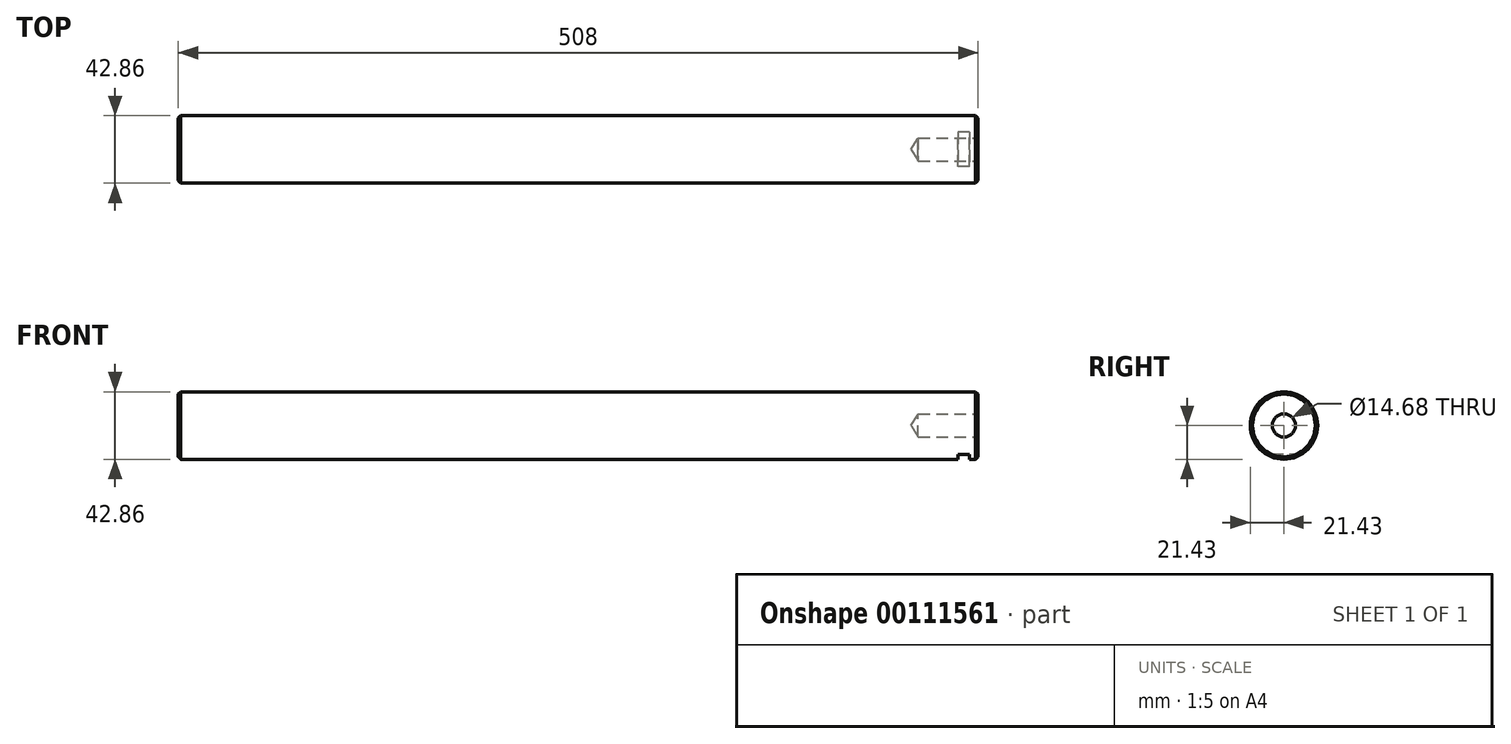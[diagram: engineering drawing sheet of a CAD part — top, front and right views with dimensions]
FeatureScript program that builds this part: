
annotation { "Feature Type Name" : "Feature", "Feature Type Description" : "" }
export const myFeature = defineFeature(function(context is Context, id is Id, definition is map)
    precondition{}
    {
        {
            var Q0;
            Q0=qCreatedBy(makeId("Right.planeOp"),FACE);
            var sketch = newSketch(context, id + "F0", { "sketchPlane" : qUnion([Q0])});
            skCircle(sketch, "E0", {"center": v(0, 0) * mm, "radius": 21.43 * mm});
            skSolve(sketch);
        }
        {
            var Q0;
            Q0 = qSketchRegion(id + "F0", true);
            extrude(context, id + "F1", {"entities" : qUnion([Q0]), "endBound" : BoundingType.SYMMETRIC, "depth" : 508 * mm});
        }
        {
            var Q0;
            Q0=makeQuery(id+"F1.opExtrude","CAP_FACE",FACE,{"disambiguationData":[OSD([sQuery(id+"F0.wireOp",EDGE,"E0")])],"isStart":false});
            var Q1;
            Q1=makeQuery(id+"F1.opExtrude","CAP_FACE",FACE,{"disambiguationData":[OSD([sQuery(id+"F0.wireOp",EDGE,"E0")])],"isStart":true});
            chamfer(context, id + "F2", {"entities" : qUnion([Q0, Q1]), "width" : 1.52 * mm, "tangentPropagation" : true});
        }
        {
            var Q0;
            Q0=makeQuery(id+"F1.opExtrude","CAP_FACE",FACE,{"disambiguationData":[OSD([sQuery(id+"F0.wireOp",EDGE,"E0")])],"isStart":false});
            var sketch = newSketch(context, id + "F3", { "sketchPlane" : qUnion([Q0])});
            skPoint(sketch, "E1", {"position": v(0, 0) * mm});
            skSolve(sketch);
        }
        {
            var Q0;
            Q0=sQuery(id+"F3.wireOp",VERTEX,"E1");
            var Q1;
            Q1=makeQuery(id+"F1.opExtrude","SWEPT_BODY",BODY,{"disambiguationData":[OSD([sQuery(id+"F0.wireOp",EDGE,"E0")])]});
            hole(context, id + "F4", {"style" : HoleStyle.SIMPLE, "endStyle" : HoleEndStyle.BLIND, "standardTappedOrClearance" : lookupTablePath({ "standard" : "ANSI", "engagement" : "75%", "pitch" : "18 tpi", "size" : "5/8", "type" : "Tapped" }), "standardBlindInLast" : lookupTablePath({ "standard" : "ANSI", "engagement" : "75%", "pitch" : "18 tpi", "size" : "5/8", "type" : "Tapped" }), "holeDiameter" : 14.68 * mm, "holeDepth" : 38.1 * mm, "locations" : qUnion([Q0]), "scope" : qUnion([Q1]), "majorDiameter" : 15.88 * mm});
        }
        {
            var Q0;
            Q0=qCreatedBy(makeId("Front.planeOp"),FACE);
            cPlane(context, id + "F5", {"entities" : qUnion([Q0]), "cplaneType" : CPlaneType.OFFSET, "offset" : 21.43 * mm, "width" : 152.4 * mm, "height" : 152.4 * mm});
        }
        {
            var Q0;
            Q0=qCreatedBy(id+"F5.planeOp",FACE);
            var sketch = newSketch(context, id + "F6", { "sketchPlane" : qUnion([Q0])});
            skLineSegment(sketch, "E2.0", {"start": v(254, 19.9) * mm, "end": v(254, -19.9) * mm, "construction": true});
            skLineSegment(sketch, "E3.0", {"start": v(241.3, 19.9) * mm, "end": v(241.3, -21.43) * mm, "construction": true});
            skLineSegment(sketch, "E4", {"start": v(252.48, -21.43) * mm, "end": v(-252.48, -21.43) * mm, "construction": true});
            skLineSegment(sketch, "E5.bottom", {"start": v(241.3, -21.43) * mm, "end": v(248.41, -21.43) * mm});
            skLineSegment(sketch, "E5.top", {"start": v(241.3, -18.38) * mm, "end": v(248.41, -18.38) * mm});
            skLineSegment(sketch, "E5.left", {"start": v(241.3, -21.43) * mm, "end": v(241.3, -18.38) * mm});
            skLineSegment(sketch, "E5.right", {"start": v(248.41, -21.43) * mm, "end": v(248.41, -18.38) * mm});
            skSolve(sketch);
        }
        {
            var Q0;
            Q0 = qSketchRegion(id + "F6", true);
            extrude(context, id + "F7", {"entities" : qUnion([Q0]), "operationType" : NewBodyOperationType.REMOVE, "endBound" : BoundingType.THROUGH_ALL, "oppositeDirection" : true, "depth" : 25.4 * mm});
        }
    });
